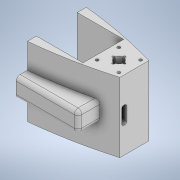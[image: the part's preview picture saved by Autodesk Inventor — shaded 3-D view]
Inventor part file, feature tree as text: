
AUTODESK INVENTOR PART (.ipt)
format: ipt  version: 2020.3 (Build 243373000, 373)  size: 780,800 bytes
history: native  units: mm
features: sketch x18, extrude x16, fillet x14, loft x1
ambient origin geometry x8: Origin, YZ Plane, XZ Plane, XY Plane, X Axis, Y Axis, Z Axis, Center Point
bodies: Solid1 (feature_tree)
feature tree (49):
  extrude  "Extrusion1"  Depth=10.0mm
  extrude  "Extrusion2"  Depth=3.0mm
  extrude  "Extrusion3"  Depth=40.0mm
  extrude  "Extrusion4"  Depth=10.0mm
  extrude  "Extrusion5"  Depth=42.2mm
  extrude  "Extrusion6"  Depth=10.0mm
  fillet  "Fillet1"  Radius=44.052mm
  fillet  "Fillet2"  Radius=10.0mm
  fillet  "Fillet3"  Radius=47.2mm
  extrude  "Extrusion7"  Depth=18.0mm TaperAngle=0.0deg
  extrude  "Extrusion8"  Depth=10.0mm
  sketch  "Sketch9"  dims[d67=0.926mm d68=48.2mm d69=44.052mm d70=10.0mm d71=0.0mm d72=47.2mm d73=0.0mm]
  extrude  "Extrusion10"  Depth=42.2mm
  extrude  "Extrusion11"  Depth=6.0mm
  loft  "Loft2"
  extrude  "Extrusion17"  Depth=7.0mm
  extrude  "Extrusion19"  Depth=2.0mm
  sketch  "Sketch25"  dims[d126=0.0mm d127=0.0mm d128=7.0mm]
  sketch  "Sketch27"  dims[d129=2.0mm d130=2.0mm]
  extrude  "Extrusion22"  Depth=21.2mm
  extrude  "Extrusion23"  Depth=0.5mm
  sketch  "Sketch33"  dims[d136=37.0mm d137=5.0mm d138=8.0mm d139=5.0mm d140=8.0mm d141=31.0mm d142=14.0mm d143=10.0mm d147=40.0mm d148=142.0mm d149=30.0mm d150=70.0mm d151=30.0mm d152=10.0mm d153=50.0mm d154=45.0mm d155=45.0mm d156=45.0mm d157=45.0mm d158=20.0mm d159=360.0deg d160=3.0mm d161=3.0mm d162=3.0mm d163=3.0mm d164=2.65mm d165=26.0mm d166=0.0mm d178=14.0mm d179=12.0mm d182=3.0mm d183=0.0mm d184=12.0mm d185=12.0mm d186=2.0mm d187=27.0mm d188=5.0mm d189=18.0mm d190=0.0mm d191=90.0deg d192=0.0mm d193=90.0deg d246=10.0mm d247=0.0mm d251=26.0mm d252=20.0mm d253=20.0mm d254=64.0mm d255=0.0mm d294=10.0mm d295=0.0mm d296=20.0mm d297=20.0mm d298=4.0mm d299=5.0mm d300=4.0mm d301=3.0mm d302=28.5mm d303=0.0mm d304=10.0mm d305=0.0mm d306=10.0mm d307=0.0mm d309=4.0mm d310=4.0mm d311=4.0mm d312=4.0mm d313=4.0mm d314=4.0mm d315=4.0mm d316=10.0mm d318=2.0mm d319=4.0mm d320=0.5mm d109=0.5mm d110=0.872665mm d317=0.872665mm]
  extrude  "Extrusion24"  Depth=0.5mm
  extrude  "Extrusion25"  Depth=0.5mm
  fillet  "Fillet20"  Radius=8.0mm
  fillet  "Fillet21"  Radius=31.0mm
  fillet  "Fillet22"  Radius=14.0mm
  fillet  "Fillet23"  Radius=10.0mm
  fillet  "Fillet24"  Radius=26.0mm
  fillet  "Fillet25"  Radius=14.0mm
  fillet  "Fillet26"  Radius=12.0mm
  fillet  "Fillet27"  Radius=3.0mm
  fillet  "Fillet29"  Radius=12.0mm
  fillet  "Fillet30"  Radius=12.0mm
  fillet  "Fillet31"  Radius=2.0mm
  sketch  "Sketch1"  dims[d13=72.0mm d14=0.0mm]
  sketch  "Sketch2"  dims[d15=142.0mm d16=30.0mm d17=70.0mm d18=30.0mm d19=10.0mm d20=50.0mm d21=45.0mm d22=45.0mm d23=45.0mm d24=45.0mm d25=32.0mm]
  sketch  "Sketch3"  dims[d26=142.0mm d27=30.0mm d28=70.0mm d29=30.0mm d30=10.0mm d31=50.0mm d32=45.0mm d33=45.0mm d34=45.0mm d35=45.0mm]
  sketch  "Sketch4"  dims[d37=40.0mm d38=20.0mm d39=360.0deg d40=3.0mm d41=3.0mm d42=3.0mm d43=3.0mm d44=2.65mm]
  sketch  "Sketch5"  dims[d46=40.0mm d48=40.0mm]
  sketch  "Sketch6"  dims[d50=40.0mm d51=26.0mm d52=0.0mm]
  sketch  "Sketch7"  dims[d53=142.0mm d54=30.0mm d56=30.0mm d57=10.0mm d58=50.0mm d59=45.0mm d60=45.0mm d61=45.0mm d62=45.0mm d63=32.0mm d64=21.1mm]
  sketch  "Sketch8"  dims[d65=42.2mm d66=42.2mm]
  sketch  "Sketch10"  dims[d107=0.0mm d108=0.0mm d112=18.0mm d113=0.0mm]
  sketch  "Sketch13"  dims[d114=3.0mm d115=10.0mm]
  sketch  "Sketch14"  dims[d116=2.0mm d119=42.2mm]
  sketch  "Sketch22"  dims[d120=42.2mm d121=6.0mm]
  sketch  "Sketch24"  dims[d122=10.0mm d123=0.0mm d125=10.0mm]
  sketch  "Sketch32"  dims[d131=40.0mm d133=360.0deg d135=21.2mm]
